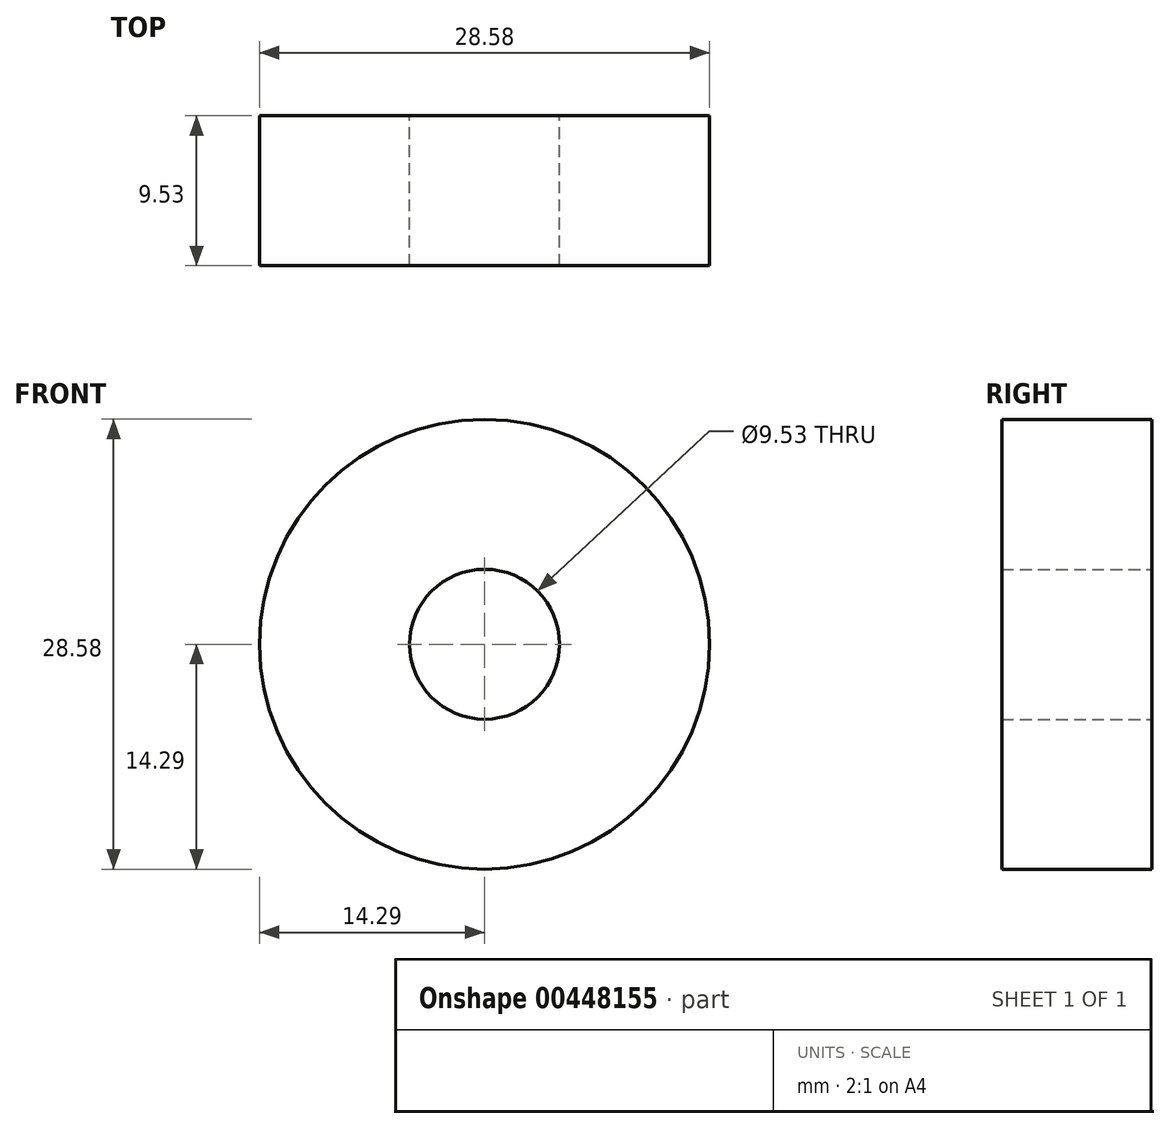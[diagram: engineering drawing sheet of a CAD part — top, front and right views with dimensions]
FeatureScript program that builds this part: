
annotation { "Feature Type Name" : "Feature", "Feature Type Description" : "" }
export const myFeature = defineFeature(function(context is Context, id is Id, definition is map)
    precondition{}
    {
        {
            var Q0;
            Q0=qCreatedBy(makeId("Front.planeOp"),FACE);
            var sketch = newSketch(context, id + "F0", { "sketchPlane" : qUnion([Q0])});
            skCircle(sketch, "E0", {"center": v(0, 0) * mm, "radius": 4.76 * mm});
            skCircle(sketch, "E1", {"center": v(0, 0) * mm, "radius": 14.29 * mm});
            skSolve(sketch);
        }
        {
            var Q0;
            Q0=makeQuery(id+"F0.imprint","IMPRINT",FACE,{"disambiguationData":[TD([[makeQuery(id+"F0.imprint","IMPRINT",EDGE,{"derivedFrom":sQuery(id+"F0.wireOp",EDGE,"E0")}),-1.0]])]});
            extrude(context, id + "F1", {"entities" : qUnion([Q0]), "depth" : 9.52 * mm});
        }
    });
